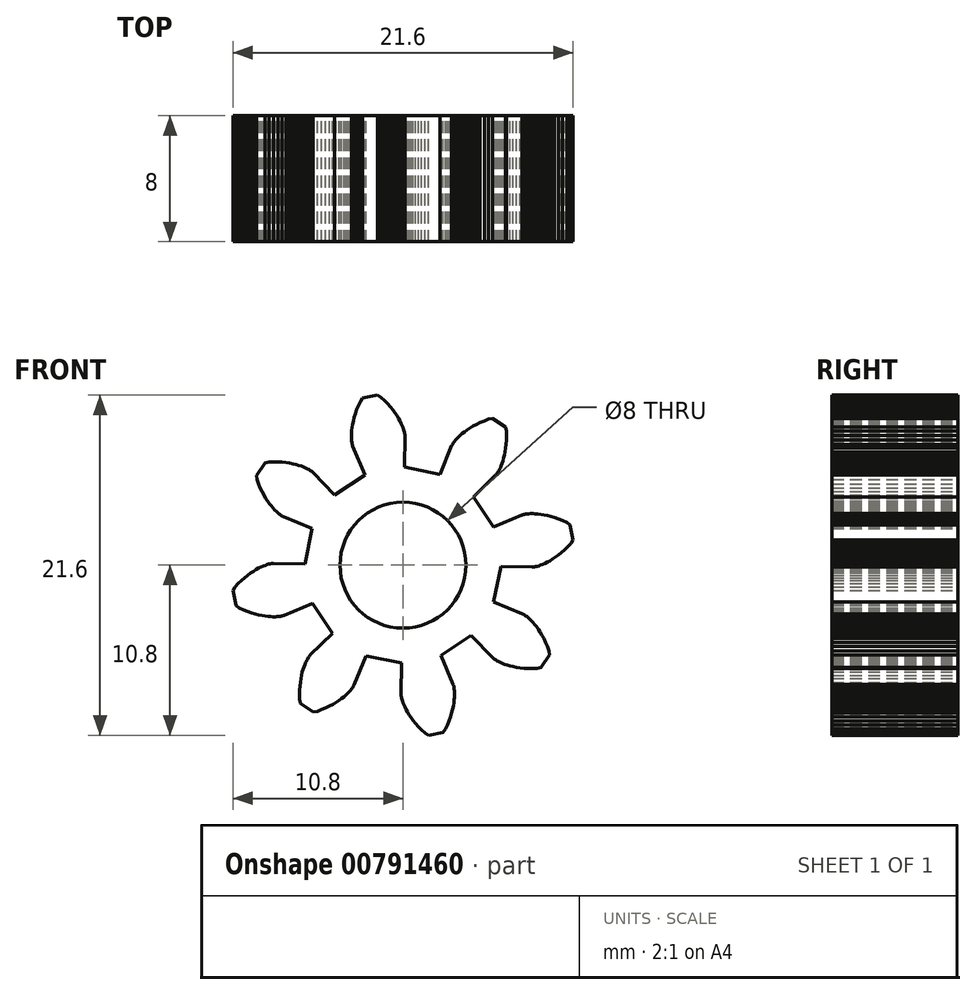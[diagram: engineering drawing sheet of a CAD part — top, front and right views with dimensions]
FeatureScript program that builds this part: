
annotation { "Feature Type Name" : "Feature", "Feature Type Description" : "" }
export const myFeature = defineFeature(function(context is Context, id is Id, definition is map)
    precondition{}
    {
        {
            var Q0;
            Q0=qCreatedBy(makeId("Front.planeOp"),FACE);
            var sketch = newSketch(context, id + "F0", { "sketchPlane" : qUnion([Q0])});
            skLineSegment(sketch, "E0", {"start": v(-6.22, 0.1) * mm, "end": v(-8.2, 0.12) * mm});
            skLineSegment(sketch, "E1", {"start": v(-8.2, 0.12) * mm, "end": v(-8.22, 0.12) * mm});
            skLineSegment(sketch, "E2", {"start": v(-8.22, 0.12) * mm, "end": v(-8.25, 0.12) * mm});
            skLineSegment(sketch, "E3", {"start": v(-8.25, 0.12) * mm, "end": v(-8.3, 0.11) * mm});
            skLineSegment(sketch, "E4", {"start": v(-8.3, 0.11) * mm, "end": v(-8.36, 0.1) * mm});
            skLineSegment(sketch, "E5", {"start": v(-8.36, 0.1) * mm, "end": v(-8.43, 0.1) * mm});
            skLineSegment(sketch, "E6", {"start": v(-8.43, 0.1) * mm, "end": v(-8.52, 0.07) * mm});
            skLineSegment(sketch, "E7", {"start": v(-8.52, 0.07) * mm, "end": v(-8.62, 0.04) * mm});
            skLineSegment(sketch, "E8", {"start": v(-8.62, 0.04) * mm, "end": v(-8.74, 0) * mm});
            skLineSegment(sketch, "E9", {"start": v(-8.74, 0) * mm, "end": v(-8.87, -0.05) * mm});
            skLineSegment(sketch, "E10", {"start": v(-8.87, -0.05) * mm, "end": v(-9.01, -0.12) * mm});
            skLineSegment(sketch, "E11", {"start": v(-9.01, -0.12) * mm, "end": v(-9.16, -0.2) * mm});
            skLineSegment(sketch, "E12", {"start": v(-9.16, -0.2) * mm, "end": v(-9.33, -0.28) * mm});
            skLineSegment(sketch, "E13", {"start": v(-9.33, -0.28) * mm, "end": v(-9.5, -0.39) * mm});
            skLineSegment(sketch, "E14", {"start": v(-9.5, -0.39) * mm, "end": v(-9.68, -0.5) * mm});
            skLineSegment(sketch, "E15", {"start": v(-9.68, -0.5) * mm, "end": v(-9.87, -0.65) * mm});
            skLineSegment(sketch, "E16", {"start": v(-9.87, -0.65) * mm, "end": v(-10.06, -0.8) * mm});
            skLineSegment(sketch, "E17", {"start": v(-10.06, -0.8) * mm, "end": v(-10.26, -0.98) * mm});
            skLineSegment(sketch, "E18", {"start": v(-10.26, -0.98) * mm, "end": v(-10.46, -1.17) * mm});
            skLineSegment(sketch, "E19", {"start": v(-10.46, -1.17) * mm, "end": v(-10.66, -1.38) * mm});
            skLineSegment(sketch, "E20", {"start": v(-10.66, -1.38) * mm, "end": v(-10.8, -1.6) * mm});
            skLineSegment(sketch, "E21", {"start": v(-10.8, -1.6) * mm, "end": v(-10.61, -2.55) * mm});
            skLineSegment(sketch, "E22", {"start": v(-10.61, -2.55) * mm, "end": v(-10.4, -2.71) * mm});
            skLineSegment(sketch, "E23", {"start": v(-10.4, -2.71) * mm, "end": v(-10.14, -2.83) * mm});
            skLineSegment(sketch, "E24", {"start": v(-10.14, -2.83) * mm, "end": v(-9.88, -2.94) * mm});
            skLineSegment(sketch, "E25", {"start": v(-9.88, -2.94) * mm, "end": v(-9.63, -3.02) * mm});
            skLineSegment(sketch, "E26", {"start": v(-9.63, -3.02) * mm, "end": v(-9.39, -3.1) * mm});
            skLineSegment(sketch, "E27", {"start": v(-9.39, -3.1) * mm, "end": v(-9.16, -3.16) * mm});
            skLineSegment(sketch, "E28", {"start": v(-9.16, -3.16) * mm, "end": v(-8.95, -3.2) * mm});
            skLineSegment(sketch, "E29", {"start": v(-8.95, -3.2) * mm, "end": v(-8.75, -3.23) * mm});
            skLineSegment(sketch, "E30", {"start": v(-8.75, -3.23) * mm, "end": v(-8.57, -3.26) * mm});
            skLineSegment(sketch, "E31", {"start": v(-8.57, -3.26) * mm, "end": v(-8.4, -3.27) * mm});
            skLineSegment(sketch, "E32", {"start": v(-8.4, -3.27) * mm, "end": v(-8.24, -3.27) * mm});
            skLineSegment(sketch, "E33", {"start": v(-8.24, -3.27) * mm, "end": v(-8.1, -3.27) * mm});
            skLineSegment(sketch, "E34", {"start": v(-8.1, -3.27) * mm, "end": v(-7.98, -3.27) * mm});
            skLineSegment(sketch, "E35", {"start": v(-7.98, -3.27) * mm, "end": v(-7.87, -3.25) * mm});
            skLineSegment(sketch, "E36", {"start": v(-7.87, -3.25) * mm, "end": v(-7.78, -3.24) * mm});
            skLineSegment(sketch, "E37", {"start": v(-7.78, -3.24) * mm, "end": v(-7.7, -3.23) * mm});
            skLineSegment(sketch, "E38", {"start": v(-7.7, -3.23) * mm, "end": v(-7.65, -3.21) * mm});
            skLineSegment(sketch, "E39", {"start": v(-7.65, -3.21) * mm, "end": v(-7.6, -3.2) * mm});
            skLineSegment(sketch, "E40", {"start": v(-7.6, -3.2) * mm, "end": v(-7.58, -3.2) * mm});
            skLineSegment(sketch, "E41", {"start": v(-7.58, -3.2) * mm, "end": v(-7.56, -3.19) * mm});
            skLineSegment(sketch, "E42", {"start": v(-7.56, -3.19) * mm, "end": v(-5.73, -2.42) * mm});
            skLineSegment(sketch, "E43", {"start": v(-5.73, -2.42) * mm, "end": v(-4.47, -4.33) * mm});
            skLineSegment(sketch, "E44", {"start": v(-4.47, -4.33) * mm, "end": v(-5.89, -5.72) * mm});
            skLineSegment(sketch, "E45", {"start": v(-5.89, -5.72) * mm, "end": v(-5.9, -5.73) * mm});
            skLineSegment(sketch, "E46", {"start": v(-5.9, -5.73) * mm, "end": v(-5.92, -5.75) * mm});
            skLineSegment(sketch, "E47", {"start": v(-5.92, -5.75) * mm, "end": v(-5.95, -5.78) * mm});
            skLineSegment(sketch, "E48", {"start": v(-5.95, -5.78) * mm, "end": v(-5.98, -5.83) * mm});
            skLineSegment(sketch, "E49", {"start": v(-5.98, -5.83) * mm, "end": v(-6.03, -5.9) * mm});
            skLineSegment(sketch, "E50", {"start": v(-6.03, -5.9) * mm, "end": v(-6.07, -5.98) * mm});
            skLineSegment(sketch, "E51", {"start": v(-6.07, -5.98) * mm, "end": v(-6.12, -6.07) * mm});
            skLineSegment(sketch, "E52", {"start": v(-6.12, -6.07) * mm, "end": v(-6.18, -6.18) * mm});
            skLineSegment(sketch, "E53", {"start": v(-6.18, -6.18) * mm, "end": v(-6.23, -6.3) * mm});
            skLineSegment(sketch, "E54", {"start": v(-6.23, -6.3) * mm, "end": v(-6.3, -6.45) * mm});
            skLineSegment(sketch, "E55", {"start": v(-6.3, -6.45) * mm, "end": v(-6.34, -6.62) * mm});
            skLineSegment(sketch, "E56", {"start": v(-6.34, -6.62) * mm, "end": v(-6.4, -6.8) * mm});
            skLineSegment(sketch, "E57", {"start": v(-6.4, -6.8) * mm, "end": v(-6.44, -6.99) * mm});
            skLineSegment(sketch, "E58", {"start": v(-6.44, -6.99) * mm, "end": v(-6.48, -7.2) * mm});
            skLineSegment(sketch, "E59", {"start": v(-6.48, -7.2) * mm, "end": v(-6.52, -7.43) * mm});
            skLineSegment(sketch, "E60", {"start": v(-6.52, -7.43) * mm, "end": v(-6.55, -7.68) * mm});
            skLineSegment(sketch, "E61", {"start": v(-6.55, -7.68) * mm, "end": v(-6.56, -7.94) * mm});
            skLineSegment(sketch, "E62", {"start": v(-6.56, -7.94) * mm, "end": v(-6.57, -8.22) * mm});
            skLineSegment(sketch, "E63", {"start": v(-6.57, -8.22) * mm, "end": v(-6.56, -8.52) * mm});
            skLineSegment(sketch, "E64", {"start": v(-6.56, -8.52) * mm, "end": v(-6.5, -8.77) * mm});
            skLineSegment(sketch, "E65", {"start": v(-6.5, -8.77) * mm, "end": v(-5.7, -9.31) * mm});
            skLineSegment(sketch, "E66", {"start": v(-5.7, -9.31) * mm, "end": v(-5.44, -9.27) * mm});
            skLineSegment(sketch, "E67", {"start": v(-5.44, -9.27) * mm, "end": v(-5.16, -9.17) * mm});
            skLineSegment(sketch, "E68", {"start": v(-5.16, -9.17) * mm, "end": v(-4.9, -9.06) * mm});
            skLineSegment(sketch, "E69", {"start": v(-4.9, -9.06) * mm, "end": v(-4.67, -8.95) * mm});
            skLineSegment(sketch, "E70", {"start": v(-4.67, -8.95) * mm, "end": v(-4.45, -8.83) * mm});
            skLineSegment(sketch, "E71", {"start": v(-4.45, -8.83) * mm, "end": v(-4.25, -8.71) * mm});
            skLineSegment(sketch, "E72", {"start": v(-4.25, -8.71) * mm, "end": v(-4.07, -8.6) * mm});
            skLineSegment(sketch, "E73", {"start": v(-4.07, -8.6) * mm, "end": v(-3.9, -8.48) * mm});
            skLineSegment(sketch, "E74", {"start": v(-3.9, -8.48) * mm, "end": v(-3.76, -8.36) * mm});
            skLineSegment(sketch, "E75", {"start": v(-3.76, -8.36) * mm, "end": v(-3.63, -8.25) * mm});
            skLineSegment(sketch, "E76", {"start": v(-3.63, -8.25) * mm, "end": v(-3.51, -8.14) * mm});
            skLineSegment(sketch, "E77", {"start": v(-3.51, -8.14) * mm, "end": v(-3.42, -8.04) * mm});
            skLineSegment(sketch, "E78", {"start": v(-3.42, -8.04) * mm, "end": v(-3.33, -7.95) * mm});
            skLineSegment(sketch, "E79", {"start": v(-3.33, -7.95) * mm, "end": v(-3.27, -7.87) * mm});
            skLineSegment(sketch, "E80", {"start": v(-3.27, -7.87) * mm, "end": v(-3.21, -7.8) * mm});
            skLineSegment(sketch, "E81", {"start": v(-3.21, -7.8) * mm, "end": v(-3.17, -7.73) * mm});
            skLineSegment(sketch, "E82", {"start": v(-3.17, -7.73) * mm, "end": v(-3.14, -7.68) * mm});
            skLineSegment(sketch, "E83", {"start": v(-3.14, -7.68) * mm, "end": v(-3.11, -7.64) * mm});
            skLineSegment(sketch, "E84", {"start": v(-3.11, -7.64) * mm, "end": v(-3.1, -7.62) * mm});
            skLineSegment(sketch, "E85", {"start": v(-3.1, -7.62) * mm, "end": v(-3.1, -7.6) * mm});
            skLineSegment(sketch, "E86", {"start": v(-3.1, -7.6) * mm, "end": v(-2.35, -5.76) * mm});
            skLineSegment(sketch, "E87", {"start": v(-2.35, -5.76) * mm, "end": v(-0.1, -6.22) * mm});
            skLineSegment(sketch, "E88", {"start": v(-0.1, -6.22) * mm, "end": v(-0.12, -8.2) * mm});
            skLineSegment(sketch, "E89", {"start": v(-0.12, -8.2) * mm, "end": v(-0.12, -8.22) * mm});
            skLineSegment(sketch, "E90", {"start": v(-0.12, -8.22) * mm, "end": v(-0.12, -8.25) * mm});
            skLineSegment(sketch, "E91", {"start": v(-0.12, -8.25) * mm, "end": v(-0.11, -8.3) * mm});
            skLineSegment(sketch, "E92", {"start": v(-0.11, -8.3) * mm, "end": v(-0.1, -8.36) * mm});
            skLineSegment(sketch, "E93", {"start": v(-0.1, -8.36) * mm, "end": v(-0.1, -8.43) * mm});
            skLineSegment(sketch, "E94", {"start": v(-0.1, -8.43) * mm, "end": v(-0.07, -8.52) * mm});
            skLineSegment(sketch, "E95", {"start": v(-0.07, -8.52) * mm, "end": v(-0.04, -8.62) * mm});
            skLineSegment(sketch, "E96", {"start": v(-0.04, -8.62) * mm, "end": v(0, -8.74) * mm});
            skLineSegment(sketch, "E97", {"start": v(0, -8.74) * mm, "end": v(0.05, -8.87) * mm});
            skLineSegment(sketch, "E98", {"start": v(0.05, -8.87) * mm, "end": v(0.12, -9.01) * mm});
            skLineSegment(sketch, "E99", {"start": v(0.12, -9.01) * mm, "end": v(0.2, -9.16) * mm});
            skLineSegment(sketch, "E100", {"start": v(0.2, -9.16) * mm, "end": v(0.28, -9.33) * mm});
            skLineSegment(sketch, "E101", {"start": v(0.28, -9.33) * mm, "end": v(0.39, -9.5) * mm});
            skLineSegment(sketch, "E102", {"start": v(0.39, -9.5) * mm, "end": v(0.5, -9.68) * mm});
            skLineSegment(sketch, "E103", {"start": v(0.5, -9.68) * mm, "end": v(0.65, -9.87) * mm});
            skLineSegment(sketch, "E104", {"start": v(0.65, -9.87) * mm, "end": v(0.8, -10.06) * mm});
            skLineSegment(sketch, "E105", {"start": v(0.8, -10.06) * mm, "end": v(0.98, -10.26) * mm});
            skLineSegment(sketch, "E106", {"start": v(0.98, -10.26) * mm, "end": v(1.17, -10.46) * mm});
            skLineSegment(sketch, "E107", {"start": v(1.17, -10.46) * mm, "end": v(1.38, -10.66) * mm});
            skLineSegment(sketch, "E108", {"start": v(1.38, -10.66) * mm, "end": v(1.6, -10.8) * mm});
            skLineSegment(sketch, "E109", {"start": v(1.6, -10.8) * mm, "end": v(2.55, -10.61) * mm});
            skLineSegment(sketch, "E110", {"start": v(2.55, -10.61) * mm, "end": v(2.71, -10.4) * mm});
            skLineSegment(sketch, "E111", {"start": v(2.71, -10.4) * mm, "end": v(2.83, -10.14) * mm});
            skLineSegment(sketch, "E112", {"start": v(2.83, -10.14) * mm, "end": v(2.94, -9.88) * mm});
            skLineSegment(sketch, "E113", {"start": v(2.94, -9.88) * mm, "end": v(3.02, -9.63) * mm});
            skLineSegment(sketch, "E114", {"start": v(3.02, -9.63) * mm, "end": v(3.1, -9.39) * mm});
            skLineSegment(sketch, "E115", {"start": v(3.1, -9.39) * mm, "end": v(3.16, -9.16) * mm});
            skLineSegment(sketch, "E116", {"start": v(3.16, -9.16) * mm, "end": v(3.2, -8.95) * mm});
            skLineSegment(sketch, "E117", {"start": v(3.2, -8.95) * mm, "end": v(3.23, -8.75) * mm});
            skLineSegment(sketch, "E118", {"start": v(3.23, -8.75) * mm, "end": v(3.26, -8.57) * mm});
            skLineSegment(sketch, "E119", {"start": v(3.26, -8.57) * mm, "end": v(3.27, -8.4) * mm});
            skLineSegment(sketch, "E120", {"start": v(3.27, -8.4) * mm, "end": v(3.27, -8.24) * mm});
            skLineSegment(sketch, "E121", {"start": v(3.27, -8.24) * mm, "end": v(3.27, -8.1) * mm});
            skLineSegment(sketch, "E122", {"start": v(3.27, -8.1) * mm, "end": v(3.27, -7.98) * mm});
            skLineSegment(sketch, "E123", {"start": v(3.27, -7.98) * mm, "end": v(3.25, -7.87) * mm});
            skLineSegment(sketch, "E124", {"start": v(3.25, -7.87) * mm, "end": v(3.24, -7.78) * mm});
            skLineSegment(sketch, "E125", {"start": v(3.24, -7.78) * mm, "end": v(3.23, -7.7) * mm});
            skLineSegment(sketch, "E126", {"start": v(3.23, -7.7) * mm, "end": v(3.21, -7.65) * mm});
            skLineSegment(sketch, "E127", {"start": v(3.21, -7.65) * mm, "end": v(3.2, -7.6) * mm});
            skLineSegment(sketch, "E128", {"start": v(3.2, -7.6) * mm, "end": v(3.2, -7.58) * mm});
            skLineSegment(sketch, "E129", {"start": v(3.2, -7.58) * mm, "end": v(3.19, -7.56) * mm});
            skLineSegment(sketch, "E130", {"start": v(3.19, -7.56) * mm, "end": v(2.42, -5.73) * mm});
            skLineSegment(sketch, "E131", {"start": v(2.42, -5.73) * mm, "end": v(4.33, -4.47) * mm});
            skLineSegment(sketch, "E132", {"start": v(4.33, -4.47) * mm, "end": v(5.72, -5.89) * mm});
            skLineSegment(sketch, "E133", {"start": v(5.72, -5.89) * mm, "end": v(5.73, -5.9) * mm});
            skLineSegment(sketch, "E134", {"start": v(5.73, -5.9) * mm, "end": v(5.75, -5.92) * mm});
            skLineSegment(sketch, "E135", {"start": v(5.75, -5.92) * mm, "end": v(5.78, -5.95) * mm});
            skLineSegment(sketch, "E136", {"start": v(5.78, -5.95) * mm, "end": v(5.83, -5.98) * mm});
            skLineSegment(sketch, "E137", {"start": v(5.83, -5.98) * mm, "end": v(5.9, -6.03) * mm});
            skLineSegment(sketch, "E138", {"start": v(5.9, -6.03) * mm, "end": v(5.98, -6.07) * mm});
            skLineSegment(sketch, "E139", {"start": v(5.98, -6.07) * mm, "end": v(6.07, -6.12) * mm});
            skLineSegment(sketch, "E140", {"start": v(6.07, -6.12) * mm, "end": v(6.18, -6.18) * mm});
            skLineSegment(sketch, "E141", {"start": v(6.18, -6.18) * mm, "end": v(6.3, -6.23) * mm});
            skLineSegment(sketch, "E142", {"start": v(6.3, -6.23) * mm, "end": v(6.45, -6.3) * mm});
            skLineSegment(sketch, "E143", {"start": v(6.45, -6.3) * mm, "end": v(6.62, -6.34) * mm});
            skLineSegment(sketch, "E144", {"start": v(6.62, -6.34) * mm, "end": v(6.8, -6.4) * mm});
            skLineSegment(sketch, "E145", {"start": v(6.8, -6.4) * mm, "end": v(6.99, -6.44) * mm});
            skLineSegment(sketch, "E146", {"start": v(6.99, -6.44) * mm, "end": v(7.2, -6.48) * mm});
            skLineSegment(sketch, "E147", {"start": v(7.2, -6.48) * mm, "end": v(7.43, -6.52) * mm});
            skLineSegment(sketch, "E148", {"start": v(7.43, -6.52) * mm, "end": v(7.68, -6.55) * mm});
            skLineSegment(sketch, "E149", {"start": v(7.68, -6.55) * mm, "end": v(7.94, -6.56) * mm});
            skLineSegment(sketch, "E150", {"start": v(7.94, -6.56) * mm, "end": v(8.22, -6.57) * mm});
            skLineSegment(sketch, "E151", {"start": v(8.22, -6.57) * mm, "end": v(8.52, -6.56) * mm});
            skLineSegment(sketch, "E152", {"start": v(8.52, -6.56) * mm, "end": v(8.77, -6.5) * mm});
            skLineSegment(sketch, "E153", {"start": v(8.77, -6.5) * mm, "end": v(9.31, -5.7) * mm});
            skLineSegment(sketch, "E154", {"start": v(9.31, -5.7) * mm, "end": v(9.27, -5.44) * mm});
            skLineSegment(sketch, "E155", {"start": v(9.27, -5.44) * mm, "end": v(9.17, -5.16) * mm});
            skLineSegment(sketch, "E156", {"start": v(9.17, -5.16) * mm, "end": v(9.06, -4.9) * mm});
            skLineSegment(sketch, "E157", {"start": v(9.06, -4.9) * mm, "end": v(8.95, -4.67) * mm});
            skLineSegment(sketch, "E158", {"start": v(8.95, -4.67) * mm, "end": v(8.83, -4.45) * mm});
            skLineSegment(sketch, "E159", {"start": v(8.83, -4.45) * mm, "end": v(8.71, -4.25) * mm});
            skLineSegment(sketch, "E160", {"start": v(8.71, -4.25) * mm, "end": v(8.6, -4.07) * mm});
            skLineSegment(sketch, "E161", {"start": v(8.6, -4.07) * mm, "end": v(8.48, -3.9) * mm});
            skLineSegment(sketch, "E162", {"start": v(8.48, -3.9) * mm, "end": v(8.36, -3.76) * mm});
            skLineSegment(sketch, "E163", {"start": v(8.36, -3.76) * mm, "end": v(8.25, -3.63) * mm});
            skLineSegment(sketch, "E164", {"start": v(8.25, -3.63) * mm, "end": v(8.14, -3.51) * mm});
            skLineSegment(sketch, "E165", {"start": v(8.14, -3.51) * mm, "end": v(8.04, -3.42) * mm});
            skLineSegment(sketch, "E166", {"start": v(8.04, -3.42) * mm, "end": v(7.95, -3.33) * mm});
            skLineSegment(sketch, "E167", {"start": v(7.95, -3.33) * mm, "end": v(7.87, -3.27) * mm});
            skLineSegment(sketch, "E168", {"start": v(7.87, -3.27) * mm, "end": v(7.8, -3.21) * mm});
            skLineSegment(sketch, "E169", {"start": v(7.8, -3.21) * mm, "end": v(7.73, -3.17) * mm});
            skLineSegment(sketch, "E170", {"start": v(7.73, -3.17) * mm, "end": v(7.68, -3.14) * mm});
            skLineSegment(sketch, "E171", {"start": v(7.68, -3.14) * mm, "end": v(7.64, -3.11) * mm});
            skLineSegment(sketch, "E172", {"start": v(7.64, -3.11) * mm, "end": v(7.62, -3.1) * mm});
            skLineSegment(sketch, "E173", {"start": v(7.62, -3.1) * mm, "end": v(7.6, -3.1) * mm});
            skLineSegment(sketch, "E174", {"start": v(7.6, -3.1) * mm, "end": v(5.76, -2.35) * mm});
            skLineSegment(sketch, "E175", {"start": v(5.76, -2.35) * mm, "end": v(6.22, -0.1) * mm});
            skLineSegment(sketch, "E176", {"start": v(6.22, -0.1) * mm, "end": v(8.2, -0.12) * mm});
            skLineSegment(sketch, "E177", {"start": v(8.2, -0.12) * mm, "end": v(8.22, -0.12) * mm});
            skLineSegment(sketch, "E178", {"start": v(8.22, -0.12) * mm, "end": v(8.25, -0.12) * mm});
            skLineSegment(sketch, "E179", {"start": v(8.25, -0.12) * mm, "end": v(8.3, -0.11) * mm});
            skLineSegment(sketch, "E180", {"start": v(8.3, -0.11) * mm, "end": v(8.36, -0.1) * mm});
            skLineSegment(sketch, "E181", {"start": v(8.36, -0.1) * mm, "end": v(8.43, -0.1) * mm});
            skLineSegment(sketch, "E182", {"start": v(8.43, -0.1) * mm, "end": v(8.52, -0.07) * mm});
            skLineSegment(sketch, "E183", {"start": v(8.52, -0.07) * mm, "end": v(8.62, -0.04) * mm});
            skLineSegment(sketch, "E184", {"start": v(8.62, -0.04) * mm, "end": v(8.74, 0) * mm});
            skLineSegment(sketch, "E185", {"start": v(8.74, 0) * mm, "end": v(8.87, 0.05) * mm});
            skLineSegment(sketch, "E186", {"start": v(8.87, 0.05) * mm, "end": v(9.01, 0.12) * mm});
            skLineSegment(sketch, "E187", {"start": v(9.01, 0.12) * mm, "end": v(9.16, 0.2) * mm});
            skLineSegment(sketch, "E188", {"start": v(9.16, 0.2) * mm, "end": v(9.33, 0.28) * mm});
            skLineSegment(sketch, "E189", {"start": v(9.33, 0.28) * mm, "end": v(9.5, 0.39) * mm});
            skLineSegment(sketch, "E190", {"start": v(9.5, 0.39) * mm, "end": v(9.68, 0.5) * mm});
            skLineSegment(sketch, "E191", {"start": v(9.68, 0.5) * mm, "end": v(9.87, 0.65) * mm});
            skLineSegment(sketch, "E192", {"start": v(9.87, 0.65) * mm, "end": v(10.06, 0.8) * mm});
            skLineSegment(sketch, "E193", {"start": v(10.06, 0.8) * mm, "end": v(10.26, 0.98) * mm});
            skLineSegment(sketch, "E194", {"start": v(10.26, 0.98) * mm, "end": v(10.46, 1.17) * mm});
            skLineSegment(sketch, "E195", {"start": v(10.46, 1.17) * mm, "end": v(10.66, 1.38) * mm});
            skLineSegment(sketch, "E196", {"start": v(10.66, 1.38) * mm, "end": v(10.8, 1.6) * mm});
            skLineSegment(sketch, "E197", {"start": v(10.8, 1.6) * mm, "end": v(10.61, 2.55) * mm});
            skLineSegment(sketch, "E198", {"start": v(10.61, 2.55) * mm, "end": v(10.4, 2.71) * mm});
            skLineSegment(sketch, "E199", {"start": v(10.4, 2.71) * mm, "end": v(10.14, 2.83) * mm});
            skLineSegment(sketch, "E200", {"start": v(10.14, 2.83) * mm, "end": v(9.88, 2.94) * mm});
            skLineSegment(sketch, "E201", {"start": v(9.88, 2.94) * mm, "end": v(9.63, 3.02) * mm});
            skLineSegment(sketch, "E202", {"start": v(9.63, 3.02) * mm, "end": v(9.39, 3.1) * mm});
            skLineSegment(sketch, "E203", {"start": v(9.39, 3.1) * mm, "end": v(9.16, 3.16) * mm});
            skLineSegment(sketch, "E204", {"start": v(9.16, 3.16) * mm, "end": v(8.95, 3.2) * mm});
            skLineSegment(sketch, "E205", {"start": v(8.95, 3.2) * mm, "end": v(8.75, 3.23) * mm});
            skLineSegment(sketch, "E206", {"start": v(8.75, 3.23) * mm, "end": v(8.57, 3.26) * mm});
            skLineSegment(sketch, "E207", {"start": v(8.57, 3.26) * mm, "end": v(8.4, 3.27) * mm});
            skLineSegment(sketch, "E208", {"start": v(8.4, 3.27) * mm, "end": v(8.24, 3.27) * mm});
            skLineSegment(sketch, "E209", {"start": v(8.24, 3.27) * mm, "end": v(8.1, 3.27) * mm});
            skLineSegment(sketch, "E210", {"start": v(8.1, 3.27) * mm, "end": v(7.98, 3.27) * mm});
            skLineSegment(sketch, "E211", {"start": v(7.98, 3.27) * mm, "end": v(7.87, 3.25) * mm});
            skLineSegment(sketch, "E212", {"start": v(7.87, 3.25) * mm, "end": v(7.78, 3.24) * mm});
            skLineSegment(sketch, "E213", {"start": v(7.78, 3.24) * mm, "end": v(7.7, 3.23) * mm});
            skLineSegment(sketch, "E214", {"start": v(7.7, 3.23) * mm, "end": v(7.65, 3.21) * mm});
            skLineSegment(sketch, "E215", {"start": v(7.65, 3.21) * mm, "end": v(7.6, 3.2) * mm});
            skLineSegment(sketch, "E216", {"start": v(7.6, 3.2) * mm, "end": v(7.58, 3.2) * mm});
            skLineSegment(sketch, "E217", {"start": v(7.58, 3.2) * mm, "end": v(7.56, 3.19) * mm});
            skLineSegment(sketch, "E218", {"start": v(7.56, 3.19) * mm, "end": v(5.73, 2.42) * mm});
            skLineSegment(sketch, "E219", {"start": v(5.73, 2.42) * mm, "end": v(4.47, 4.33) * mm});
            skLineSegment(sketch, "E220", {"start": v(4.47, 4.33) * mm, "end": v(5.89, 5.72) * mm});
            skLineSegment(sketch, "E221", {"start": v(5.89, 5.72) * mm, "end": v(5.9, 5.73) * mm});
            skLineSegment(sketch, "E222", {"start": v(5.9, 5.73) * mm, "end": v(5.92, 5.75) * mm});
            skLineSegment(sketch, "E223", {"start": v(5.92, 5.75) * mm, "end": v(5.95, 5.78) * mm});
            skLineSegment(sketch, "E224", {"start": v(5.95, 5.78) * mm, "end": v(5.98, 5.83) * mm});
            skLineSegment(sketch, "E225", {"start": v(5.98, 5.83) * mm, "end": v(6.03, 5.9) * mm});
            skLineSegment(sketch, "E226", {"start": v(6.03, 5.9) * mm, "end": v(6.07, 5.98) * mm});
            skLineSegment(sketch, "E227", {"start": v(6.07, 5.98) * mm, "end": v(6.12, 6.07) * mm});
            skLineSegment(sketch, "E228", {"start": v(6.12, 6.07) * mm, "end": v(6.18, 6.18) * mm});
            skLineSegment(sketch, "E229", {"start": v(6.18, 6.18) * mm, "end": v(6.23, 6.3) * mm});
            skLineSegment(sketch, "E230", {"start": v(6.23, 6.3) * mm, "end": v(6.3, 6.45) * mm});
            skLineSegment(sketch, "E231", {"start": v(6.3, 6.45) * mm, "end": v(6.34, 6.62) * mm});
            skLineSegment(sketch, "E232", {"start": v(6.34, 6.62) * mm, "end": v(6.4, 6.8) * mm});
            skLineSegment(sketch, "E233", {"start": v(6.4, 6.8) * mm, "end": v(6.44, 6.99) * mm});
            skLineSegment(sketch, "E234", {"start": v(6.44, 6.99) * mm, "end": v(6.48, 7.2) * mm});
            skLineSegment(sketch, "E235", {"start": v(6.48, 7.2) * mm, "end": v(6.52, 7.43) * mm});
            skLineSegment(sketch, "E236", {"start": v(6.52, 7.43) * mm, "end": v(6.55, 7.68) * mm});
            skLineSegment(sketch, "E237", {"start": v(6.55, 7.68) * mm, "end": v(6.56, 7.94) * mm});
            skLineSegment(sketch, "E238", {"start": v(6.56, 7.94) * mm, "end": v(6.57, 8.22) * mm});
            skLineSegment(sketch, "E239", {"start": v(6.57, 8.22) * mm, "end": v(6.56, 8.52) * mm});
            skLineSegment(sketch, "E240", {"start": v(6.56, 8.52) * mm, "end": v(6.5, 8.77) * mm});
            skLineSegment(sketch, "E241", {"start": v(6.5, 8.77) * mm, "end": v(5.7, 9.31) * mm});
            skLineSegment(sketch, "E242", {"start": v(5.7, 9.31) * mm, "end": v(5.44, 9.27) * mm});
            skLineSegment(sketch, "E243", {"start": v(5.44, 9.27) * mm, "end": v(5.16, 9.17) * mm});
            skLineSegment(sketch, "E244", {"start": v(5.16, 9.17) * mm, "end": v(4.9, 9.06) * mm});
            skLineSegment(sketch, "E245", {"start": v(4.9, 9.06) * mm, "end": v(4.67, 8.95) * mm});
            skLineSegment(sketch, "E246", {"start": v(4.67, 8.95) * mm, "end": v(4.45, 8.83) * mm});
            skLineSegment(sketch, "E247", {"start": v(4.45, 8.83) * mm, "end": v(4.25, 8.71) * mm});
            skLineSegment(sketch, "E248", {"start": v(4.25, 8.71) * mm, "end": v(4.07, 8.6) * mm});
            skLineSegment(sketch, "E249", {"start": v(4.07, 8.6) * mm, "end": v(3.9, 8.48) * mm});
            skLineSegment(sketch, "E250", {"start": v(3.9, 8.48) * mm, "end": v(3.76, 8.36) * mm});
            skLineSegment(sketch, "E251", {"start": v(3.76, 8.36) * mm, "end": v(3.63, 8.25) * mm});
            skLineSegment(sketch, "E252", {"start": v(3.63, 8.25) * mm, "end": v(3.51, 8.14) * mm});
            skLineSegment(sketch, "E253", {"start": v(3.51, 8.14) * mm, "end": v(3.42, 8.04) * mm});
            skLineSegment(sketch, "E254", {"start": v(3.42, 8.04) * mm, "end": v(3.33, 7.95) * mm});
            skLineSegment(sketch, "E255", {"start": v(3.33, 7.95) * mm, "end": v(3.27, 7.87) * mm});
            skLineSegment(sketch, "E256", {"start": v(3.27, 7.87) * mm, "end": v(3.21, 7.8) * mm});
            skLineSegment(sketch, "E257", {"start": v(3.21, 7.8) * mm, "end": v(3.17, 7.73) * mm});
            skLineSegment(sketch, "E258", {"start": v(3.17, 7.73) * mm, "end": v(3.14, 7.68) * mm});
            skLineSegment(sketch, "E259", {"start": v(3.14, 7.68) * mm, "end": v(3.11, 7.64) * mm});
            skLineSegment(sketch, "E260", {"start": v(3.11, 7.64) * mm, "end": v(3.1, 7.62) * mm});
            skLineSegment(sketch, "E261", {"start": v(3.1, 7.62) * mm, "end": v(3.1, 7.6) * mm});
            skLineSegment(sketch, "E262", {"start": v(3.1, 7.6) * mm, "end": v(2.35, 5.76) * mm});
            skLineSegment(sketch, "E263", {"start": v(2.35, 5.76) * mm, "end": v(0.1, 6.22) * mm});
            skLineSegment(sketch, "E264", {"start": v(0.1, 6.22) * mm, "end": v(0.12, 8.2) * mm});
            skLineSegment(sketch, "E265", {"start": v(0.12, 8.2) * mm, "end": v(0.12, 8.22) * mm});
            skLineSegment(sketch, "E266", {"start": v(0.12, 8.22) * mm, "end": v(0.12, 8.25) * mm});
            skLineSegment(sketch, "E267", {"start": v(0.12, 8.25) * mm, "end": v(0.11, 8.3) * mm});
            skLineSegment(sketch, "E268", {"start": v(0.11, 8.3) * mm, "end": v(0.1, 8.36) * mm});
            skLineSegment(sketch, "E269", {"start": v(0.1, 8.36) * mm, "end": v(0.1, 8.43) * mm});
            skLineSegment(sketch, "E270", {"start": v(0.1, 8.43) * mm, "end": v(0.07, 8.52) * mm});
            skLineSegment(sketch, "E271", {"start": v(0.07, 8.52) * mm, "end": v(0.04, 8.62) * mm});
            skLineSegment(sketch, "E272", {"start": v(0.04, 8.62) * mm, "end": v(0, 8.74) * mm});
            skLineSegment(sketch, "E273", {"start": v(0, 8.74) * mm, "end": v(-0.05, 8.87) * mm});
            skLineSegment(sketch, "E274", {"start": v(-0.05, 8.87) * mm, "end": v(-0.12, 9.01) * mm});
            skLineSegment(sketch, "E275", {"start": v(-0.12, 9.01) * mm, "end": v(-0.2, 9.16) * mm});
            skLineSegment(sketch, "E276", {"start": v(-0.2, 9.16) * mm, "end": v(-0.28, 9.33) * mm});
            skLineSegment(sketch, "E277", {"start": v(-0.28, 9.33) * mm, "end": v(-0.39, 9.5) * mm});
            skLineSegment(sketch, "E278", {"start": v(-0.39, 9.5) * mm, "end": v(-0.5, 9.68) * mm});
            skLineSegment(sketch, "E279", {"start": v(-0.5, 9.68) * mm, "end": v(-0.65, 9.87) * mm});
            skLineSegment(sketch, "E280", {"start": v(-0.65, 9.87) * mm, "end": v(-0.8, 10.06) * mm});
            skLineSegment(sketch, "E281", {"start": v(-0.8, 10.06) * mm, "end": v(-0.98, 10.26) * mm});
            skLineSegment(sketch, "E282", {"start": v(-0.98, 10.26) * mm, "end": v(-1.17, 10.46) * mm});
            skLineSegment(sketch, "E283", {"start": v(-1.17, 10.46) * mm, "end": v(-1.38, 10.66) * mm});
            skLineSegment(sketch, "E284", {"start": v(-1.38, 10.66) * mm, "end": v(-1.6, 10.8) * mm});
            skLineSegment(sketch, "E285", {"start": v(-1.6, 10.8) * mm, "end": v(-2.55, 10.61) * mm});
            skLineSegment(sketch, "E286", {"start": v(-2.55, 10.61) * mm, "end": v(-2.71, 10.4) * mm});
            skLineSegment(sketch, "E287", {"start": v(-2.71, 10.4) * mm, "end": v(-2.83, 10.14) * mm});
            skLineSegment(sketch, "E288", {"start": v(-2.83, 10.14) * mm, "end": v(-2.94, 9.88) * mm});
            skLineSegment(sketch, "E289", {"start": v(-2.94, 9.88) * mm, "end": v(-3.02, 9.63) * mm});
            skLineSegment(sketch, "E290", {"start": v(-3.02, 9.63) * mm, "end": v(-3.1, 9.39) * mm});
            skLineSegment(sketch, "E291", {"start": v(-3.1, 9.39) * mm, "end": v(-3.16, 9.16) * mm});
            skLineSegment(sketch, "E292", {"start": v(-3.16, 9.16) * mm, "end": v(-3.2, 8.95) * mm});
            skLineSegment(sketch, "E293", {"start": v(-3.2, 8.95) * mm, "end": v(-3.23, 8.75) * mm});
            skLineSegment(sketch, "E294", {"start": v(-3.23, 8.75) * mm, "end": v(-3.26, 8.57) * mm});
            skLineSegment(sketch, "E295", {"start": v(-3.26, 8.57) * mm, "end": v(-3.27, 8.4) * mm});
            skLineSegment(sketch, "E296", {"start": v(-3.27, 8.4) * mm, "end": v(-3.27, 8.24) * mm});
            skLineSegment(sketch, "E297", {"start": v(-3.27, 8.24) * mm, "end": v(-3.27, 8.1) * mm});
            skLineSegment(sketch, "E298", {"start": v(-3.27, 8.1) * mm, "end": v(-3.27, 7.98) * mm});
            skLineSegment(sketch, "E299", {"start": v(-3.27, 7.98) * mm, "end": v(-3.25, 7.87) * mm});
            skLineSegment(sketch, "E300", {"start": v(-3.25, 7.87) * mm, "end": v(-3.24, 7.78) * mm});
            skLineSegment(sketch, "E301", {"start": v(-3.24, 7.78) * mm, "end": v(-3.23, 7.7) * mm});
            skLineSegment(sketch, "E302", {"start": v(-3.23, 7.7) * mm, "end": v(-3.21, 7.65) * mm});
            skLineSegment(sketch, "E303", {"start": v(-3.21, 7.65) * mm, "end": v(-3.2, 7.6) * mm});
            skLineSegment(sketch, "E304", {"start": v(-3.2, 7.6) * mm, "end": v(-3.2, 7.58) * mm});
            skLineSegment(sketch, "E305", {"start": v(-3.2, 7.58) * mm, "end": v(-3.19, 7.56) * mm});
            skLineSegment(sketch, "E306", {"start": v(-3.19, 7.56) * mm, "end": v(-2.42, 5.73) * mm});
            skLineSegment(sketch, "E307", {"start": v(-2.42, 5.73) * mm, "end": v(-4.33, 4.47) * mm});
            skLineSegment(sketch, "E308", {"start": v(-4.33, 4.47) * mm, "end": v(-5.72, 5.89) * mm});
            skLineSegment(sketch, "E309", {"start": v(-5.72, 5.89) * mm, "end": v(-5.73, 5.9) * mm});
            skLineSegment(sketch, "E310", {"start": v(-5.73, 5.9) * mm, "end": v(-5.75, 5.92) * mm});
            skLineSegment(sketch, "E311", {"start": v(-5.75, 5.92) * mm, "end": v(-5.78, 5.95) * mm});
            skLineSegment(sketch, "E312", {"start": v(-5.78, 5.95) * mm, "end": v(-5.83, 5.98) * mm});
            skLineSegment(sketch, "E313", {"start": v(-5.83, 5.98) * mm, "end": v(-5.9, 6.03) * mm});
            skLineSegment(sketch, "E314", {"start": v(-5.9, 6.03) * mm, "end": v(-5.98, 6.07) * mm});
            skLineSegment(sketch, "E315", {"start": v(-5.98, 6.07) * mm, "end": v(-6.07, 6.12) * mm});
            skLineSegment(sketch, "E316", {"start": v(-6.07, 6.12) * mm, "end": v(-6.18, 6.18) * mm});
            skLineSegment(sketch, "E317", {"start": v(-6.18, 6.18) * mm, "end": v(-6.3, 6.23) * mm});
            skLineSegment(sketch, "E318", {"start": v(-6.3, 6.23) * mm, "end": v(-6.45, 6.3) * mm});
            skLineSegment(sketch, "E319", {"start": v(-6.45, 6.3) * mm, "end": v(-6.62, 6.34) * mm});
            skLineSegment(sketch, "E320", {"start": v(-6.62, 6.34) * mm, "end": v(-6.8, 6.4) * mm});
            skLineSegment(sketch, "E321", {"start": v(-6.8, 6.4) * mm, "end": v(-6.99, 6.44) * mm});
            skLineSegment(sketch, "E322", {"start": v(-6.99, 6.44) * mm, "end": v(-7.2, 6.48) * mm});
            skLineSegment(sketch, "E323", {"start": v(-7.2, 6.48) * mm, "end": v(-7.43, 6.52) * mm});
            skLineSegment(sketch, "E324", {"start": v(-7.43, 6.52) * mm, "end": v(-7.68, 6.55) * mm});
            skLineSegment(sketch, "E325", {"start": v(-7.68, 6.55) * mm, "end": v(-7.94, 6.56) * mm});
            skLineSegment(sketch, "E326", {"start": v(-7.94, 6.56) * mm, "end": v(-8.22, 6.57) * mm});
            skLineSegment(sketch, "E327", {"start": v(-8.22, 6.57) * mm, "end": v(-8.52, 6.56) * mm});
            skLineSegment(sketch, "E328", {"start": v(-8.52, 6.56) * mm, "end": v(-8.77, 6.5) * mm});
            skLineSegment(sketch, "E329", {"start": v(-8.77, 6.5) * mm, "end": v(-9.31, 5.7) * mm});
            skLineSegment(sketch, "E330", {"start": v(-9.31, 5.7) * mm, "end": v(-9.27, 5.44) * mm});
            skLineSegment(sketch, "E331", {"start": v(-9.27, 5.44) * mm, "end": v(-9.17, 5.16) * mm});
            skLineSegment(sketch, "E332", {"start": v(-9.17, 5.16) * mm, "end": v(-9.06, 4.9) * mm});
            skLineSegment(sketch, "E333", {"start": v(-9.06, 4.9) * mm, "end": v(-8.95, 4.67) * mm});
            skLineSegment(sketch, "E334", {"start": v(-8.95, 4.67) * mm, "end": v(-8.83, 4.45) * mm});
            skLineSegment(sketch, "E335", {"start": v(-8.83, 4.45) * mm, "end": v(-8.71, 4.25) * mm});
            skLineSegment(sketch, "E336", {"start": v(-8.71, 4.25) * mm, "end": v(-8.6, 4.07) * mm});
            skLineSegment(sketch, "E337", {"start": v(-8.6, 4.07) * mm, "end": v(-8.48, 3.9) * mm});
            skLineSegment(sketch, "E338", {"start": v(-8.48, 3.9) * mm, "end": v(-8.36, 3.76) * mm});
            skLineSegment(sketch, "E339", {"start": v(-8.36, 3.76) * mm, "end": v(-8.25, 3.63) * mm});
            skLineSegment(sketch, "E340", {"start": v(-8.25, 3.63) * mm, "end": v(-8.14, 3.51) * mm});
            skLineSegment(sketch, "E341", {"start": v(-8.14, 3.51) * mm, "end": v(-8.04, 3.42) * mm});
            skLineSegment(sketch, "E342", {"start": v(-8.04, 3.42) * mm, "end": v(-7.95, 3.33) * mm});
            skLineSegment(sketch, "E343", {"start": v(-7.95, 3.33) * mm, "end": v(-7.87, 3.27) * mm});
            skLineSegment(sketch, "E344", {"start": v(-7.87, 3.27) * mm, "end": v(-7.8, 3.21) * mm});
            skLineSegment(sketch, "E345", {"start": v(-7.8, 3.21) * mm, "end": v(-7.73, 3.17) * mm});
            skLineSegment(sketch, "E346", {"start": v(-7.73, 3.17) * mm, "end": v(-7.68, 3.14) * mm});
            skLineSegment(sketch, "E347", {"start": v(-7.68, 3.14) * mm, "end": v(-7.64, 3.11) * mm});
            skLineSegment(sketch, "E348", {"start": v(-7.64, 3.11) * mm, "end": v(-7.62, 3.1) * mm});
            skLineSegment(sketch, "E349", {"start": v(-7.62, 3.1) * mm, "end": v(-7.6, 3.1) * mm});
            skLineSegment(sketch, "E350", {"start": v(-7.6, 3.1) * mm, "end": v(-5.76, 2.35) * mm});
            skLineSegment(sketch, "E351", {"start": v(-5.76, 2.35) * mm, "end": v(-6.22, 0.1) * mm});
            skCircle(sketch, "E352", {"center": v(0, 0) * mm, "radius": 8.73 * mm, "construction": true});
            skCircle(sketch, "E353", {"center": v(0, 0) * mm, "radius": 4 * mm});
            skSolve(sketch);
        }
        {
            var Q0;
            Q0 = qSketchRegion(id + "F0", true);
            extrude(context, id + "F1", {"entities" : qUnion([Q0]), "depth" : 8 * mm, "offsetDistance" : 25 * mm});
        }
    });
